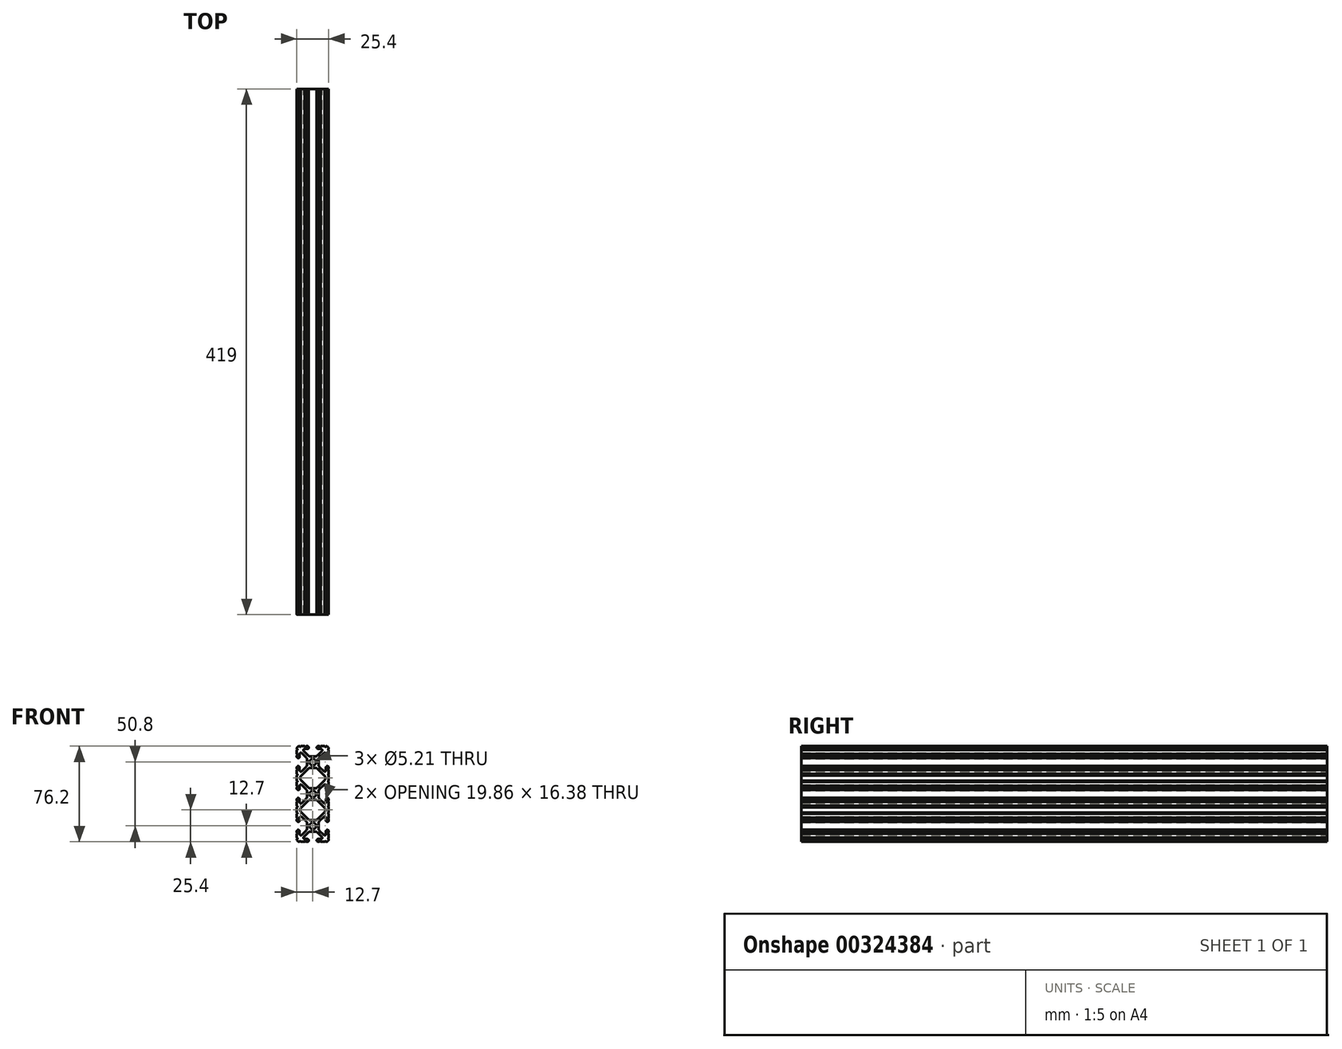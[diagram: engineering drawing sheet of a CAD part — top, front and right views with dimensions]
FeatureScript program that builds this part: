
annotation { "Feature Type Name" : "Feature", "Feature Type Description" : "" }
export const myFeature = defineFeature(function(context is Context, id is Id, definition is map)
    precondition{}
    {
        {
            var Q0;
            Q0=qCreatedBy(makeId("Front.planeOp"),FACE);
            var sketch = newSketch(context, id + "F0", { "sketchPlane" : qUnion([Q0])});
            skArc(sketch, "E0", {"start": v(2.6, 25.4) * mm, "mid": v(0, 28) * mm, "end": v(-2.6, 25.4) * mm});
            skArc(sketch, "E1", {"start": v(-2.6, 25.4) * mm, "mid": v(0, 22.8) * mm, "end": v(2.6, 25.4) * mm});
            skArc(sketch, "E2", {"start": v(-10.57, 38.1) * mm, "mid": v(-10.06, 37.6) * mm, "end": v(-9.55, 38.1) * mm});
            skArc(sketch, "E3", {"start": v(-10.57, 38.1) * mm, "mid": v(-12.08, 37.48) * mm, "end": v(-12.7, 35.97) * mm});
            skArc(sketch, "E4", {"start": v(-12.7, 34.95) * mm, "mid": v(-12.2, 35.46) * mm, "end": v(-12.7, 35.97) * mm});
            skLineSegment(sketch, "E5", {"start": v(-12.7, 34.95) * mm, "end": v(-12.7, 31.72) * mm});
            skArc(sketch, "E6", {"start": v(-12.7, 30.7) * mm, "mid": v(-12.2, 31.22) * mm, "end": v(-12.7, 31.72) * mm});
            skLineSegment(sketch, "E7", {"start": v(-12.7, 30.7) * mm, "end": v(-12.7, 29.7) * mm});
            skArc(sketch, "E8", {"start": v(-12.7, 29.7) * mm, "mid": v(-11.6, 28.6) * mm, "end": v(-10.5, 29.7) * mm});
            skLineSegment(sketch, "E9", {"start": v(-10.5, 29.7) * mm, "end": v(-10.5, 31.87) * mm});
            skArc(sketch, "E10", {"start": v(-8.76, 32.6) * mm, "mid": v(-9.86, 32.81) * mm, "end": v(-10.5, 31.87) * mm});
            skLineSegment(sketch, "E11", {"start": v(-8.76, 32.6) * mm, "end": v(-5.44, 29.28) * mm});
            skArc(sketch, "E12", {"start": v(-4.5, 27.03) * mm, "mid": v(-4.75, 28.25) * mm, "end": v(-5.44, 29.28) * mm});
            skLineSegment(sketch, "E13", {"start": v(-4.5, 27.03) * mm, "end": v(-4.5, 23.77) * mm});
            skArc(sketch, "E14", {"start": v(-5.44, 21.52) * mm, "mid": v(-4.75, 22.55) * mm, "end": v(-4.5, 23.77) * mm});
            skLineSegment(sketch, "E15", {"start": v(-5.44, 21.52) * mm, "end": v(-8.76, 18.2) * mm});
            skArc(sketch, "E16", {"start": v(-10.5, 18.93) * mm, "mid": v(-9.86, 17.99) * mm, "end": v(-8.76, 18.2) * mm});
            skLineSegment(sketch, "E17", {"start": v(-10.5, 18.93) * mm, "end": v(-10.5, 21.1) * mm});
            skArc(sketch, "E18", {"start": v(-10.5, 21.1) * mm, "mid": v(-11.6, 22.2) * mm, "end": v(-12.7, 21.1) * mm});
            skLineSegment(sketch, "E19", {"start": v(-12.7, 21.1) * mm, "end": v(-12.7, 20.1) * mm});
            skArc(sketch, "E20", {"start": v(-12.7, 19.08) * mm, "mid": v(-12.2, 19.58) * mm, "end": v(-12.7, 20.1) * mm});
            skLineSegment(sketch, "E21", {"start": v(-12.7, 19.08) * mm, "end": v(-12.7, 15.85) * mm});
            skArc(sketch, "E22", {"start": v(-12.7, 14.83) * mm, "mid": v(-12.2, 15.34) * mm, "end": v(-12.7, 15.85) * mm});
            skLineSegment(sketch, "E23", {"start": v(-12.7, 14.83) * mm, "end": v(-12.7, 10.57) * mm});
            skArc(sketch, "E24", {"start": v(-12.7, 9.55) * mm, "mid": v(-12.2, 10.06) * mm, "end": v(-12.7, 10.57) * mm});
            skLineSegment(sketch, "E25", {"start": v(-12.7, 9.55) * mm, "end": v(-12.7, 6.32) * mm});
            skArc(sketch, "E26", {"start": v(-12.7, 5.3) * mm, "mid": v(-12.2, 5.82) * mm, "end": v(-12.7, 6.32) * mm});
            skLineSegment(sketch, "E27", {"start": v(-12.7, 5.3) * mm, "end": v(-12.7, 4.3) * mm});
            skArc(sketch, "E28", {"start": v(-12.7, 4.3) * mm, "mid": v(-11.6, 3.2) * mm, "end": v(-10.5, 4.3) * mm});
            skLineSegment(sketch, "E29", {"start": v(-10.5, 4.3) * mm, "end": v(-10.5, 6.47) * mm});
            skArc(sketch, "E30", {"start": v(-8.76, 7.2) * mm, "mid": v(-9.86, 7.41) * mm, "end": v(-10.5, 6.47) * mm});
            skLineSegment(sketch, "E31", {"start": v(-8.76, 7.2) * mm, "end": v(-5.44, 3.88) * mm});
            skArc(sketch, "E32", {"start": v(-4.5, 1.63) * mm, "mid": v(-4.75, 2.85) * mm, "end": v(-5.44, 3.88) * mm});
            skLineSegment(sketch, "E33", {"start": v(-4.5, 1.63) * mm, "end": v(-4.5, -1.63) * mm});
            skArc(sketch, "E34", {"start": v(-5.44, -3.88) * mm, "mid": v(-4.75, -2.85) * mm, "end": v(-4.5, -1.63) * mm});
            skLineSegment(sketch, "E35", {"start": v(-5.44, -3.88) * mm, "end": v(-8.76, -7.2) * mm});
            skArc(sketch, "E36", {"start": v(-10.5, -6.47) * mm, "mid": v(-9.86, -7.41) * mm, "end": v(-8.76, -7.2) * mm});
            skLineSegment(sketch, "E37", {"start": v(-10.5, -6.47) * mm, "end": v(-10.5, -4.3) * mm});
            skArc(sketch, "E38", {"start": v(-10.5, -4.3) * mm, "mid": v(-11.6, -3.2) * mm, "end": v(-12.7, -4.3) * mm});
            skLineSegment(sketch, "E39", {"start": v(-12.7, -4.3) * mm, "end": v(-12.7, -5.3) * mm});
            skArc(sketch, "E40", {"start": v(-12.7, -6.32) * mm, "mid": v(-12.2, -5.82) * mm, "end": v(-12.7, -5.3) * mm});
            skLineSegment(sketch, "E41", {"start": v(-12.7, -6.32) * mm, "end": v(-12.7, -9.55) * mm});
            skArc(sketch, "E42", {"start": v(-12.7, -10.57) * mm, "mid": v(-12.2, -10.06) * mm, "end": v(-12.7, -9.55) * mm});
            skLineSegment(sketch, "E43", {"start": v(-12.7, -10.57) * mm, "end": v(-12.7, -14.83) * mm});
            skArc(sketch, "E44", {"start": v(-12.7, -15.85) * mm, "mid": v(-12.2, -15.34) * mm, "end": v(-12.7, -14.83) * mm});
            skLineSegment(sketch, "E45", {"start": v(-12.7, -15.85) * mm, "end": v(-12.7, -19.08) * mm});
            skArc(sketch, "E46", {"start": v(-12.7, -20.1) * mm, "mid": v(-12.2, -19.58) * mm, "end": v(-12.7, -19.08) * mm});
            skLineSegment(sketch, "E47", {"start": v(-12.7, -20.1) * mm, "end": v(-12.7, -21.1) * mm});
            skArc(sketch, "E48", {"start": v(-12.7, -21.1) * mm, "mid": v(-11.6, -22.2) * mm, "end": v(-10.5, -21.1) * mm});
            skLineSegment(sketch, "E49", {"start": v(-10.5, -21.1) * mm, "end": v(-10.5, -18.93) * mm});
            skArc(sketch, "E50", {"start": v(-8.76, -18.2) * mm, "mid": v(-9.86, -17.99) * mm, "end": v(-10.5, -18.93) * mm});
            skLineSegment(sketch, "E51", {"start": v(-8.76, -18.2) * mm, "end": v(-5.44, -21.52) * mm});
            skArc(sketch, "E52", {"start": v(-4.5, -23.77) * mm, "mid": v(-4.75, -22.55) * mm, "end": v(-5.44, -21.52) * mm});
            skLineSegment(sketch, "E53", {"start": v(-4.5, -23.77) * mm, "end": v(-4.5, -27.03) * mm});
            skArc(sketch, "E54", {"start": v(-5.44, -29.28) * mm, "mid": v(-4.75, -28.25) * mm, "end": v(-4.5, -27.03) * mm});
            skLineSegment(sketch, "E55", {"start": v(-5.44, -29.28) * mm, "end": v(-8.76, -32.6) * mm});
            skArc(sketch, "E56", {"start": v(-10.5, -31.87) * mm, "mid": v(-9.86, -32.81) * mm, "end": v(-8.76, -32.6) * mm});
            skLineSegment(sketch, "E57", {"start": v(-10.5, -31.87) * mm, "end": v(-10.5, -29.7) * mm});
            skArc(sketch, "E58", {"start": v(-10.5, -29.7) * mm, "mid": v(-11.6, -28.6) * mm, "end": v(-12.7, -29.7) * mm});
            skLineSegment(sketch, "E59", {"start": v(-12.7, -29.7) * mm, "end": v(-12.7, -30.7) * mm});
            skArc(sketch, "E60", {"start": v(-12.7, -31.72) * mm, "mid": v(-12.2, -31.22) * mm, "end": v(-12.7, -30.7) * mm});
            skLineSegment(sketch, "E61", {"start": v(-12.7, -31.72) * mm, "end": v(-12.7, -34.95) * mm});
            skArc(sketch, "E62", {"start": v(-12.7, -35.97) * mm, "mid": v(-12.2, -35.46) * mm, "end": v(-12.7, -34.95) * mm});
            skArc(sketch, "E63", {"start": v(-12.7, -35.97) * mm, "mid": v(-12.08, -37.48) * mm, "end": v(-10.57, -38.1) * mm});
            skArc(sketch, "E64", {"start": v(-9.55, -38.1) * mm, "mid": v(-10.06, -37.6) * mm, "end": v(-10.57, -38.1) * mm});
            skLineSegment(sketch, "E65", {"start": v(-9.55, -38.1) * mm, "end": v(-6.32, -38.1) * mm});
            skArc(sketch, "E66", {"start": v(-5.3, -38.1) * mm, "mid": v(-5.82, -37.6) * mm, "end": v(-6.32, -38.1) * mm});
            skLineSegment(sketch, "E67", {"start": v(-5.3, -38.1) * mm, "end": v(-4.3, -38.1) * mm});
            skArc(sketch, "E68", {"start": v(-4.3, -38.1) * mm, "mid": v(-3.2, -37) * mm, "end": v(-4.3, -35.9) * mm});
            skLineSegment(sketch, "E69", {"start": v(-4.3, -35.9) * mm, "end": v(-6.47, -35.9) * mm});
            skArc(sketch, "E70", {"start": v(-7.2, -34.16) * mm, "mid": v(-7.41, -35.26) * mm, "end": v(-6.47, -35.9) * mm});
            skLineSegment(sketch, "E71", {"start": v(-7.2, -34.16) * mm, "end": v(-3.88, -30.84) * mm});
            skArc(sketch, "E72", {"start": v(-1.63, -29.9) * mm, "mid": v(-2.85, -30.15) * mm, "end": v(-3.88, -30.84) * mm});
            skLineSegment(sketch, "E73", {"start": v(-1.63, -29.9) * mm, "end": v(1.63, -29.9) * mm});
            skArc(sketch, "E74", {"start": v(3.88, -30.84) * mm, "mid": v(2.85, -30.15) * mm, "end": v(1.63, -29.9) * mm});
            skLineSegment(sketch, "E75", {"start": v(3.88, -30.84) * mm, "end": v(7.2, -34.16) * mm});
            skArc(sketch, "E76", {"start": v(6.47, -35.9) * mm, "mid": v(7.41, -35.26) * mm, "end": v(7.2, -34.16) * mm});
            skLineSegment(sketch, "E77", {"start": v(6.47, -35.9) * mm, "end": v(4.3, -35.9) * mm});
            skArc(sketch, "E78", {"start": v(4.3, -35.9) * mm, "mid": v(3.2, -37) * mm, "end": v(4.3, -38.1) * mm});
            skLineSegment(sketch, "E79", {"start": v(4.3, -38.1) * mm, "end": v(5.3, -38.1) * mm});
            skArc(sketch, "E80", {"start": v(6.32, -38.1) * mm, "mid": v(5.82, -37.6) * mm, "end": v(5.3, -38.1) * mm});
            skLineSegment(sketch, "E81", {"start": v(6.32, -38.1) * mm, "end": v(9.55, -38.1) * mm});
            skArc(sketch, "E82", {"start": v(10.57, -38.1) * mm, "mid": v(10.06, -37.6) * mm, "end": v(9.55, -38.1) * mm});
            skArc(sketch, "E83", {"start": v(10.57, -38.1) * mm, "mid": v(12.08, -37.48) * mm, "end": v(12.7, -35.97) * mm});
            skArc(sketch, "E84", {"start": v(12.7, -34.95) * mm, "mid": v(12.2, -35.46) * mm, "end": v(12.7, -35.97) * mm});
            skLineSegment(sketch, "E85", {"start": v(12.7, -34.95) * mm, "end": v(12.7, -31.72) * mm});
            skArc(sketch, "E86", {"start": v(12.7, -30.7) * mm, "mid": v(12.2, -31.22) * mm, "end": v(12.7, -31.72) * mm});
            skLineSegment(sketch, "E87", {"start": v(12.7, -30.7) * mm, "end": v(12.7, -29.7) * mm});
            skArc(sketch, "E88", {"start": v(12.7, -29.7) * mm, "mid": v(11.6, -28.6) * mm, "end": v(10.5, -29.7) * mm});
            skLineSegment(sketch, "E89", {"start": v(10.5, -29.7) * mm, "end": v(10.5, -31.87) * mm});
            skArc(sketch, "E90", {"start": v(8.76, -32.6) * mm, "mid": v(9.86, -32.81) * mm, "end": v(10.5, -31.87) * mm});
            skLineSegment(sketch, "E91", {"start": v(8.76, -32.6) * mm, "end": v(5.44, -29.28) * mm});
            skArc(sketch, "E92", {"start": v(4.5, -27.03) * mm, "mid": v(4.75, -28.25) * mm, "end": v(5.44, -29.28) * mm});
            skLineSegment(sketch, "E93", {"start": v(4.5, -27.03) * mm, "end": v(4.5, -23.77) * mm});
            skArc(sketch, "E94", {"start": v(5.44, -21.52) * mm, "mid": v(4.75, -22.55) * mm, "end": v(4.5, -23.77) * mm});
            skLineSegment(sketch, "E95", {"start": v(5.44, -21.52) * mm, "end": v(8.76, -18.2) * mm});
            skArc(sketch, "E96", {"start": v(10.5, -18.93) * mm, "mid": v(9.86, -17.99) * mm, "end": v(8.76, -18.2) * mm});
            skLineSegment(sketch, "E97", {"start": v(10.5, -18.93) * mm, "end": v(10.5, -21.1) * mm});
            skArc(sketch, "E98", {"start": v(10.5, -21.1) * mm, "mid": v(11.6, -22.2) * mm, "end": v(12.7, -21.1) * mm});
            skLineSegment(sketch, "E99", {"start": v(12.7, -21.1) * mm, "end": v(12.7, -20.1) * mm});
            skArc(sketch, "E100", {"start": v(12.7, -19.08) * mm, "mid": v(12.2, -19.58) * mm, "end": v(12.7, -20.1) * mm});
            skLineSegment(sketch, "E101", {"start": v(12.7, -19.08) * mm, "end": v(12.7, -15.85) * mm});
            skArc(sketch, "E102", {"start": v(12.7, -14.83) * mm, "mid": v(12.2, -15.34) * mm, "end": v(12.7, -15.85) * mm});
            skLineSegment(sketch, "E103", {"start": v(12.7, -14.83) * mm, "end": v(12.7, -10.57) * mm});
            skArc(sketch, "E104", {"start": v(12.7, -9.55) * mm, "mid": v(12.2, -10.06) * mm, "end": v(12.7, -10.57) * mm});
            skLineSegment(sketch, "E105", {"start": v(12.7, -9.55) * mm, "end": v(12.7, -6.32) * mm});
            skArc(sketch, "E106", {"start": v(12.7, -5.3) * mm, "mid": v(12.2, -5.82) * mm, "end": v(12.7, -6.32) * mm});
            skLineSegment(sketch, "E107", {"start": v(12.7, -5.3) * mm, "end": v(12.7, -4.3) * mm});
            skArc(sketch, "E108", {"start": v(12.7, -4.3) * mm, "mid": v(11.6, -3.2) * mm, "end": v(10.5, -4.3) * mm});
            skLineSegment(sketch, "E109", {"start": v(10.5, -4.3) * mm, "end": v(10.5, -6.47) * mm});
            skArc(sketch, "E110", {"start": v(8.76, -7.2) * mm, "mid": v(9.86, -7.41) * mm, "end": v(10.5, -6.47) * mm});
            skLineSegment(sketch, "E111", {"start": v(8.76, -7.2) * mm, "end": v(5.44, -3.88) * mm});
            skArc(sketch, "E112", {"start": v(4.5, -1.63) * mm, "mid": v(4.75, -2.85) * mm, "end": v(5.44, -3.88) * mm});
            skLineSegment(sketch, "E113", {"start": v(4.5, -1.63) * mm, "end": v(4.5, 1.63) * mm});
            skArc(sketch, "E114", {"start": v(5.44, 3.88) * mm, "mid": v(4.75, 2.85) * mm, "end": v(4.5, 1.63) * mm});
            skLineSegment(sketch, "E115", {"start": v(5.44, 3.88) * mm, "end": v(8.76, 7.2) * mm});
            skArc(sketch, "E116", {"start": v(10.5, 6.47) * mm, "mid": v(9.86, 7.41) * mm, "end": v(8.76, 7.2) * mm});
            skLineSegment(sketch, "E117", {"start": v(10.5, 6.47) * mm, "end": v(10.5, 4.3) * mm});
            skArc(sketch, "E118", {"start": v(10.5, 4.3) * mm, "mid": v(11.6, 3.2) * mm, "end": v(12.7, 4.3) * mm});
            skLineSegment(sketch, "E119", {"start": v(12.7, 4.3) * mm, "end": v(12.7, 5.3) * mm});
            skArc(sketch, "E120", {"start": v(12.7, 6.32) * mm, "mid": v(12.2, 5.82) * mm, "end": v(12.7, 5.3) * mm});
            skLineSegment(sketch, "E121", {"start": v(12.7, 6.32) * mm, "end": v(12.7, 9.55) * mm});
            skArc(sketch, "E122", {"start": v(12.7, 10.57) * mm, "mid": v(12.2, 10.06) * mm, "end": v(12.7, 9.55) * mm});
            skLineSegment(sketch, "E123", {"start": v(12.7, 10.57) * mm, "end": v(12.7, 14.83) * mm});
            skArc(sketch, "E124", {"start": v(12.7, 15.85) * mm, "mid": v(12.2, 15.34) * mm, "end": v(12.7, 14.83) * mm});
            skLineSegment(sketch, "E125", {"start": v(12.7, 15.85) * mm, "end": v(12.7, 19.08) * mm});
            skArc(sketch, "E126", {"start": v(12.7, 20.1) * mm, "mid": v(12.2, 19.58) * mm, "end": v(12.7, 19.08) * mm});
            skLineSegment(sketch, "E127", {"start": v(12.7, 20.1) * mm, "end": v(12.7, 21.1) * mm});
            skArc(sketch, "E128", {"start": v(12.7, 21.1) * mm, "mid": v(11.6, 22.2) * mm, "end": v(10.5, 21.1) * mm});
            skLineSegment(sketch, "E129", {"start": v(10.5, 21.1) * mm, "end": v(10.5, 18.93) * mm});
            skArc(sketch, "E130", {"start": v(8.76, 18.2) * mm, "mid": v(9.86, 17.99) * mm, "end": v(10.5, 18.93) * mm});
            skLineSegment(sketch, "E131", {"start": v(8.76, 18.2) * mm, "end": v(5.44, 21.52) * mm});
            skArc(sketch, "E132", {"start": v(4.5, 23.77) * mm, "mid": v(4.75, 22.55) * mm, "end": v(5.44, 21.52) * mm});
            skLineSegment(sketch, "E133", {"start": v(4.5, 23.77) * mm, "end": v(4.5, 27.03) * mm});
            skArc(sketch, "E134", {"start": v(5.44, 29.28) * mm, "mid": v(4.75, 28.25) * mm, "end": v(4.5, 27.03) * mm});
            skLineSegment(sketch, "E135", {"start": v(5.44, 29.28) * mm, "end": v(8.76, 32.6) * mm});
            skArc(sketch, "E136", {"start": v(10.5, 31.87) * mm, "mid": v(9.86, 32.81) * mm, "end": v(8.76, 32.6) * mm});
            skLineSegment(sketch, "E137", {"start": v(10.5, 31.87) * mm, "end": v(10.5, 29.7) * mm});
            skArc(sketch, "E138", {"start": v(10.5, 29.7) * mm, "mid": v(11.6, 28.6) * mm, "end": v(12.7, 29.7) * mm});
            skLineSegment(sketch, "E139", {"start": v(12.7, 29.7) * mm, "end": v(12.7, 30.7) * mm});
            skArc(sketch, "E140", {"start": v(12.7, 31.72) * mm, "mid": v(12.2, 31.22) * mm, "end": v(12.7, 30.7) * mm});
            skLineSegment(sketch, "E141", {"start": v(12.7, 31.72) * mm, "end": v(12.7, 34.95) * mm});
            skArc(sketch, "E142", {"start": v(12.7, 35.97) * mm, "mid": v(12.2, 35.46) * mm, "end": v(12.7, 34.95) * mm});
            skArc(sketch, "E143", {"start": v(12.7, 35.97) * mm, "mid": v(12.08, 37.48) * mm, "end": v(10.57, 38.1) * mm});
            skArc(sketch, "E144", {"start": v(9.55, 38.1) * mm, "mid": v(10.06, 37.6) * mm, "end": v(10.57, 38.1) * mm});
            skLineSegment(sketch, "E145", {"start": v(9.55, 38.1) * mm, "end": v(6.32, 38.1) * mm});
            skArc(sketch, "E146", {"start": v(5.3, 38.1) * mm, "mid": v(5.82, 37.6) * mm, "end": v(6.32, 38.1) * mm});
            skLineSegment(sketch, "E147", {"start": v(5.3, 38.1) * mm, "end": v(4.3, 38.1) * mm});
            skArc(sketch, "E148", {"start": v(4.3, 38.1) * mm, "mid": v(3.2, 37) * mm, "end": v(4.3, 35.9) * mm});
            skLineSegment(sketch, "E149", {"start": v(4.3, 35.9) * mm, "end": v(6.47, 35.9) * mm});
            skArc(sketch, "E150", {"start": v(7.2, 34.16) * mm, "mid": v(7.41, 35.26) * mm, "end": v(6.47, 35.9) * mm});
            skLineSegment(sketch, "E151", {"start": v(7.2, 34.16) * mm, "end": v(3.88, 30.84) * mm});
            skArc(sketch, "E152", {"start": v(1.63, 29.9) * mm, "mid": v(2.85, 30.15) * mm, "end": v(3.88, 30.84) * mm});
            skLineSegment(sketch, "E153", {"start": v(1.63, 29.9) * mm, "end": v(-1.63, 29.9) * mm});
            skArc(sketch, "E154", {"start": v(-3.88, 30.84) * mm, "mid": v(-2.85, 30.15) * mm, "end": v(-1.63, 29.9) * mm});
            skLineSegment(sketch, "E155", {"start": v(-3.88, 30.84) * mm, "end": v(-7.2, 34.16) * mm});
            skArc(sketch, "E156", {"start": v(-6.47, 35.9) * mm, "mid": v(-7.41, 35.26) * mm, "end": v(-7.2, 34.16) * mm});
            skLineSegment(sketch, "E157", {"start": v(-6.47, 35.9) * mm, "end": v(-4.3, 35.9) * mm});
            skArc(sketch, "E158", {"start": v(-4.3, 35.9) * mm, "mid": v(-3.2, 37) * mm, "end": v(-4.3, 38.1) * mm});
            skLineSegment(sketch, "E159", {"start": v(-4.3, 38.1) * mm, "end": v(-5.3, 38.1) * mm});
            skArc(sketch, "E160", {"start": v(-6.32, 38.1) * mm, "mid": v(-5.82, 37.6) * mm, "end": v(-5.3, 38.1) * mm});
            skLineSegment(sketch, "E161", {"start": v(-6.32, 38.1) * mm, "end": v(-9.55, 38.1) * mm});
            skArc(sketch, "E162", {"start": v(2.6, 0) * mm, "mid": v(0, 2.6) * mm, "end": v(-2.6, 0) * mm});
            skArc(sketch, "E163", {"start": v(-2.6, 0) * mm, "mid": v(0, -2.6) * mm, "end": v(2.6, 0) * mm});
            skArc(sketch, "E164", {"start": v(2.6, -25.4) * mm, "mid": v(0, -22.8) * mm, "end": v(-2.6, -25.4) * mm});
            skArc(sketch, "E165", {"start": v(-2.6, -25.4) * mm, "mid": v(0, -28) * mm, "end": v(2.6, -25.4) * mm});
            skLineSegment(sketch, "E166", {"start": v(-3.88, -5.44) * mm, "end": v(-9.47, -11.03) * mm});
            skArc(sketch, "E167", {"start": v(-1.63, -4.5) * mm, "mid": v(-2.85, -4.75) * mm, "end": v(-3.88, -5.44) * mm});
            skLineSegment(sketch, "E168", {"start": v(1.63, -4.5) * mm, "end": v(-1.63, -4.5) * mm});
            skArc(sketch, "E169", {"start": v(3.88, -5.44) * mm, "mid": v(2.85, -4.75) * mm, "end": v(1.63, -4.5) * mm});
            skLineSegment(sketch, "E170", {"start": v(9.47, -11.03) * mm, "end": v(3.88, -5.44) * mm});
            skArc(sketch, "E171", {"start": v(9.93, -12.15) * mm, "mid": v(9.81, -11.54) * mm, "end": v(9.47, -11.03) * mm});
            skLineSegment(sketch, "E172", {"start": v(9.93, -13.25) * mm, "end": v(9.93, -12.15) * mm});
            skArc(sketch, "E173", {"start": v(9.47, -14.37) * mm, "mid": v(9.81, -13.86) * mm, "end": v(9.93, -13.25) * mm});
            skLineSegment(sketch, "E174", {"start": v(3.88, -19.96) * mm, "end": v(9.47, -14.37) * mm});
            skArc(sketch, "E175", {"start": v(1.63, -20.9) * mm, "mid": v(2.85, -20.65) * mm, "end": v(3.88, -19.96) * mm});
            skLineSegment(sketch, "E176", {"start": v(-1.63, -20.9) * mm, "end": v(1.63, -20.9) * mm});
            skArc(sketch, "E177", {"start": v(-3.88, -19.96) * mm, "mid": v(-2.85, -20.65) * mm, "end": v(-1.63, -20.9) * mm});
            skLineSegment(sketch, "E178", {"start": v(-9.47, -14.37) * mm, "end": v(-3.88, -19.96) * mm});
            skArc(sketch, "E179", {"start": v(-9.93, -13.25) * mm, "mid": v(-9.81, -13.86) * mm, "end": v(-9.47, -14.37) * mm});
            skLineSegment(sketch, "E180", {"start": v(-9.93, -12.15) * mm, "end": v(-9.93, -13.25) * mm});
            skArc(sketch, "E181", {"start": v(-9.47, -11.03) * mm, "mid": v(-9.81, -11.54) * mm, "end": v(-9.93, -12.15) * mm});
            skLineSegment(sketch, "E182", {"start": v(-3.88, 19.96) * mm, "end": v(-9.47, 14.37) * mm});
            skArc(sketch, "E183", {"start": v(-1.63, 20.9) * mm, "mid": v(-2.85, 20.65) * mm, "end": v(-3.88, 19.96) * mm});
            skLineSegment(sketch, "E184", {"start": v(1.63, 20.9) * mm, "end": v(-1.63, 20.9) * mm});
            skArc(sketch, "E185", {"start": v(3.88, 19.96) * mm, "mid": v(2.85, 20.65) * mm, "end": v(1.63, 20.9) * mm});
            skLineSegment(sketch, "E186", {"start": v(9.47, 14.37) * mm, "end": v(3.88, 19.96) * mm});
            skArc(sketch, "E187", {"start": v(9.93, 13.25) * mm, "mid": v(9.81, 13.86) * mm, "end": v(9.47, 14.37) * mm});
            skLineSegment(sketch, "E188", {"start": v(9.93, 12.15) * mm, "end": v(9.93, 13.25) * mm});
            skArc(sketch, "E189", {"start": v(9.47, 11.03) * mm, "mid": v(9.81, 11.54) * mm, "end": v(9.93, 12.15) * mm});
            skLineSegment(sketch, "E190", {"start": v(3.88, 5.44) * mm, "end": v(9.47, 11.03) * mm});
            skArc(sketch, "E191", {"start": v(1.63, 4.5) * mm, "mid": v(2.85, 4.75) * mm, "end": v(3.88, 5.44) * mm});
            skLineSegment(sketch, "E192", {"start": v(-1.63, 4.5) * mm, "end": v(1.63, 4.5) * mm});
            skArc(sketch, "E193", {"start": v(-3.88, 5.44) * mm, "mid": v(-2.85, 4.75) * mm, "end": v(-1.63, 4.5) * mm});
            skLineSegment(sketch, "E194", {"start": v(-9.47, 11.03) * mm, "end": v(-3.88, 5.44) * mm});
            skArc(sketch, "E195", {"start": v(-9.93, 12.15) * mm, "mid": v(-9.81, 11.54) * mm, "end": v(-9.47, 11.03) * mm});
            skLineSegment(sketch, "E196", {"start": v(-9.93, 13.25) * mm, "end": v(-9.93, 12.15) * mm});
            skArc(sketch, "E197", {"start": v(-9.47, 14.37) * mm, "mid": v(-9.81, 13.86) * mm, "end": v(-9.93, 13.25) * mm});
            skSolve(sketch);
        }
        {
            var Q0;
            Q0=makeQuery(id+"F0.imprint","IMPRINT",FACE,{"disambiguationData":[TD([[makeQuery(id+"F0.imprint","IMPRINT",EDGE,{"derivedFrom":sQuery(id+"F0.wireOp",EDGE,"E0")}),-1.0]])]});
            extrude(context, id + "F1", {"entities" : qUnion([Q0]), "depth" : 419 * mm});
        }
    });
